# Revit family: Casement_36_C_Side_Hung_Standard
name_source: partatom
category: Windows
revit_build: Autodesk Revit 2014 (Build: 20130308_1515(x64)
units: mm (PartAtom-declared; Revit-internal decimal feet)

## types (12) — shared parameters
Aluminium Thickness = 1 mm  [stored 0.00328084 ft]
Bead SG Gap = 13 mm  [stored 0.0426509 ft]
Casement Dimension = 36 mm  [stored 0.11811 ft]
Custom Sash Left Width = 554 mm  [stored 1.81759 ft]
Custom Sash Right Width = 554 mm  [stored 1.81759 ft]
DG Extrusion Start = 8 mm  [stored 0.0262467 ft]
DG Gasket Finish = Double Glazing Gasket Material
DG Thickness Calc = 4 mm  [stored 0.0131234 ft]
Default Sill Height = 800 mm  [stored 2.62467 ft]
Depth Bead = 22 mm  [stored 0.0721785 ft]
Depth Mullion = 37 mm  [stored 0.121391 ft]
Description = Window 36mm, Type C side hung
Frame Center Offset = 18 mm  [stored 0.0590551 ft]
Limit Fixed Pane Width Max = 1500 mm  [stored 4.92126 ft]
Limit Fixed Pane Width Min = 200 mm  [stored 0.656168 ft]
Limit Sash Height Max = 1300 mm  [stored 4.26509 ft]
Limit Sash Height Min = 300 mm  [stored 0.984252 ft]
Limit Sash Width Max = 600 mm  [stored 1.9685 ft]
Limit Sash Width Min = 300 mm  [stored 0.984252 ft]
Limit Window Height Max = 1346 mm  [stored 4.41601 ft]
Limit Window Height Min = 346 mm
Limit Window Width Max = 2700 mm
Limit Window Width Min = 1400 mm
Manufacturer = Crealco
Max System DG One Piece Thickness = 6 mm  [stored 0.019685 ft]
Max System DG Unit Thickness = 25 mm  [stored 0.082021 ft]
Model = Casement 36
Offset Bead Center Reversed = 18 mm  [stored 0.0590551 ft]
Offset Fixed Panel Left = 600 mm  [stored 1.9685 ft]
Offset Mullion Left Side = 570 mm  [stored 1.87008 ft]
Offset Mullion Right Side = 570 mm  [stored 1.87008 ft]
Offset Sash Side = 23 mm  [stored 0.0754593 ft]
Offset Sash Top = 23 mm  [stored 0.0754593 ft]
Offset Window Exterior = 18 mm  [stored 0.0590551 ft]
SG Gasket Thickness = 6 mm  [stored 0.019685 ft]
Sash Center Offset = 15 mm  [stored 0.0492126 ft]
Sash Overlap = 7 mm  [stored 0.0229659 ft]
Sash Spacing Inner = 8 mm  [stored 0.0262467 ft]
Side Hung Left = Yes
Side Hung Right = No
URL = http://www.crealco.co.za
Wall Closure = By host
Width Bead = 15 mm  [stored 0.0492126 ft]
Width Profile = 30 mm  [stored 0.0984252 ft]
Width Sash Left = 554 mm  [stored 1.81759 ft]
Width Sash Left Opening = 524 mm  [stored 1.71916 ft]
Width Sash Right = 554 mm  [stored 1.81759 ft]
Width Sash Right Opening = 524 mm  [stored 1.71916 ft]
zero-valued in all types: Window Exterior Offset

## per-type parameters (varying)
- 36-1809SS-1000Pa: Area Pane Left=0.35 m²; Area Pane Middle=0.48 m²; Area Pane Right=0.35 m²; Clearvue Insulated LowE SHGC Value=0.485; Clearvue Insulated LowE U Value=3.57; Clearvue Insulated SHGC Value=0.532; Clearvue Insulated U Value=4.09; Clearvue SHGC Value=0.603; Custom Windload=1000 mm  [stored 3.28084 ft]; Custom Window Height=890 mm  [stored 2.91995 ft]; Custom Window Width=1790 mm; Energy Advantage SHGC Value=0.54; Energy Advantage U Value=4.75; Height=890 mm  [stored 2.91995 ft]; Height Fixed Panel Center=830 mm  [stored 2.7231 ft]; Height Sash=814 mm  [stored 2.6706 ft]; Height Sash Opening=844 mm  [stored 2.76903 ft]; Intruderprufe Insulated LowE SHGC Value=0.446; Intruderprufe Insulated LowE U Value=3.5; Intruderprufe Insulated SHGC Value=0.486; Intruderprufe Insulated U Value=3.98; Intruderprufe LowE SHGC Value=0.508; Intruderprufe LowE U Value=4.64; Intruderprufe SHGC Value=0.574; Intruderprufe U Value=6.05; Length Mullion=890 mm  [stored 2.91995 ft]; Max Pane Area=0.48 m²; Mullion Depth Windload Based=37 mm  [stored 0.121391 ft]; Sash Height=845 mm  [stored 2.77231 ft]; Width=1790 mm; Width Fixed Panel Center=590 mm; Windload Design=1000 mm  [stored 3.28084 ft]
- 36-2409SS-1000Pa: Area Pane Left=0.35 m²; Area Pane Middle=0.97 m²; Area Pane Right=0.35 m²; Clearvue Insulated LowE SHGC Value=0.515; Clearvue Insulated LowE U Value=3.31; Clearvue Insulated SHGC Value=0.565; Clearvue Insulated U Value=3.87; Clearvue SHGC Value=0.642; Custom Windload=1000 mm  [stored 3.28084 ft]; Custom Window Height=890 mm  [stored 2.91995 ft]; Custom Window Width=2390 mm; Energy Advantage SHGC Value=0.574; Energy Advantage U Value=4.58; Height=890 mm  [stored 2.91995 ft]; Height Fixed Panel Center=830 mm  [stored 2.7231 ft]; Height Sash=814 mm  [stored 2.6706 ft]; Height Sash Opening=844 mm  [stored 2.76903 ft]; Intruderprufe Insulated LowE SHGC Value=0.473; Intruderprufe Insulated LowE U Value=3.24; Intruderprufe Insulated SHGC Value=0.518; Intruderprufe Insulated U Value=3.78; Intruderprufe LowE SHGC Value=0.539; Intruderprufe LowE U Value=4.47; Intruderprufe SHGC Value=0.61; Intruderprufe U Value=6; Length Mullion=890 mm  [stored 2.91995 ft]; Max Pane Area=0.97 m²; Mullion Depth Windload Based=37 mm  [stored 0.121391 ft]; Sash Height=845 mm  [stored 2.77231 ft]; Width=2390 mm; Width Fixed Panel Center=1190 mm  [stored 3.9042 ft]; Windload Design=1000 mm  [stored 3.28084 ft]
- 36-1812SS-1000Pa: Area Pane Left=0.49 m²; Area Pane Middle=0.65 m²; Area Pane Right=0.49 m²; Clearvue Insulated LowE SHGC Value=0.504; Clearvue Insulated LowE U Value=3.42; Clearvue Insulated SHGC Value=0.554; Clearvue Insulated U Value=3.96; Clearvue SHGC Value=0.628; Custom Windload=1000 mm  [stored 3.28084 ft]; Custom Window Height=1190 mm  [stored 3.9042 ft]; Custom Window Width=1790 mm; Energy Advantage SHGC Value=0.562; Energy Advantage U Value=4.65; Height=1190 mm  [stored 3.9042 ft]; Height Fixed Panel Center=1130 mm  [stored 3.70735 ft]; Height Sash=1114 mm  [stored 3.65486 ft]; Height Sash Opening=1144 mm; Intruderprufe Insulated LowE SHGC Value=0.463; Intruderprufe Insulated LowE U Value=3.35; Intruderprufe Insulated SHGC Value=0.506; Intruderprufe Insulated U Value=3.86; Intruderprufe LowE SHGC Value=0.572; Intruderprufe LowE U Value=4.54; Intruderprufe SHGC Value=0.597; Intruderprufe U Value=6.02; Length Mullion=1190 mm  [stored 3.9042 ft]; Max Pane Area=0.65 m²; Mullion Depth Windload Based=37 mm  [stored 0.121391 ft]; Sash Height=1145 mm  [stored 3.75656 ft]; Width=1790 mm; Width Fixed Panel Center=590 mm; Windload Design=1000 mm  [stored 3.28084 ft]
- 36-2412SS-1000Pa: Area Pane Left=0.49 m²; Area Pane Middle=1.32 m²; Area Pane Right=0.49 m²; Clearvue Insulated LowE SHGC Value=0.534; Clearvue Insulated LowE U Value=3.16; Clearvue Insulated SHGC Value=0.587; Clearvue Insulated U Value=3.75; Clearvue SHGC Value=0.666; Custom Windload=1000 mm  [stored 3.28084 ft]; Custom Window Height=1190 mm  [stored 3.9042 ft]; Custom Window Width=2390 mm; Energy Advantage SHGC Value=0.596; Energy Advantage U Value=4.48; Height=1190 mm  [stored 3.9042 ft]; Height Fixed Panel Center=1130 mm  [stored 3.70735 ft]; Height Sash=1114 mm  [stored 3.65486 ft]; Height Sash Opening=1144 mm; Intruderprufe Insulated LowE SHGC Value=0.49; Intruderprufe Insulated LowE U Value=3.1; Intruderprufe Insulated SHGC Value=0.538; Intruderprufe Insulated U Value=3.66; Intruderprufe LowE SHGC Value=0.558; Intruderprufe LowE U Value=4.38; Intruderprufe SHGC Value=0.633; Intruderprufe U Value=5.97; Length Mullion=1190 mm  [stored 3.9042 ft]; Max Pane Area=1.32 m²; Mullion Depth Windload Based=37 mm  [stored 0.121391 ft]; Sash Height=1145 mm  [stored 3.75656 ft]; Width=2390 mm; Width Fixed Panel Center=1190 mm  [stored 3.9042 ft]; Windload Design=1000 mm  [stored 3.28084 ft]
- 36-1809SS-1500Pa: Area Pane Left=0.35 m²; Area Pane Middle=0.48 m²; Area Pane Right=0.35 m²; Clearvue Insulated LowE SHGC Value=0.485; Clearvue Insulated LowE U Value=3.57; Clearvue Insulated SHGC Value=0.532; Clearvue Insulated U Value=4.09; Clearvue SHGC Value=0.603; Custom Windload=1500 mm  [stored 4.92126 ft]; Custom Window Height=890 mm  [stored 2.91995 ft]; Custom Window Width=1790 mm; Energy Advantage SHGC Value=0.54; Energy Advantage U Value=4.75; Height=890 mm  [stored 2.91995 ft]; Height Fixed Panel Center=830 mm  [stored 2.7231 ft]; Height Sash=814 mm  [stored 2.6706 ft]; Height Sash Opening=844 mm  [stored 2.76903 ft]; Intruderprufe Insulated LowE SHGC Value=0.446; Intruderprufe Insulated LowE U Value=3.5; Intruderprufe Insulated SHGC Value=0.486; Intruderprufe Insulated U Value=3.98; Intruderprufe LowE SHGC Value=0.508; Intruderprufe LowE U Value=4.64; Intruderprufe SHGC Value=0.574; Intruderprufe U Value=6.05; Length Mullion=890 mm  [stored 2.91995 ft]; Max Pane Area=0.48 m²; Mullion Depth Windload Based=37 mm  [stored 0.121391 ft]; Sash Height=845 mm  [stored 2.77231 ft]; Width=1790 mm; Width Fixed Panel Center=590 mm; Windload Design=1500 mm  [stored 4.92126 ft]
- 36-1809SS-2000Pa: Area Pane Left=0.35 m²; Area Pane Middle=0.48 m²; Area Pane Right=0.35 m²; Clearvue Insulated LowE SHGC Value=0.485; Clearvue Insulated LowE U Value=3.57; Clearvue Insulated SHGC Value=0.532; Clearvue Insulated U Value=4.09; Clearvue SHGC Value=0.603; Custom Windload=2000 mm; Custom Window Height=890 mm  [stored 2.91995 ft]; Custom Window Width=1790 mm; Energy Advantage SHGC Value=0.54; Energy Advantage U Value=4.75; Height=890 mm  [stored 2.91995 ft]; Height Fixed Panel Center=830 mm  [stored 2.7231 ft]; Height Sash=814 mm  [stored 2.6706 ft]; Height Sash Opening=844 mm  [stored 2.76903 ft]; Intruderprufe Insulated LowE SHGC Value=0.446; Intruderprufe Insulated LowE U Value=3.5; Intruderprufe Insulated SHGC Value=0.486; Intruderprufe Insulated U Value=3.98; Intruderprufe LowE SHGC Value=0.508; Intruderprufe LowE U Value=4.64; Intruderprufe SHGC Value=0.574; Intruderprufe U Value=6.05; Length Mullion=890 mm  [stored 2.91995 ft]; Max Pane Area=0.48 m²; Mullion Depth Windload Based=37 mm  [stored 0.121391 ft]; Sash Height=845 mm  [stored 2.77231 ft]; Width=1790 mm; Width Fixed Panel Center=590 mm; Windload Design=2000 mm
- 36-2409SS-1500Pa: Area Pane Left=0.35 m²; Area Pane Middle=0.97 m²; Area Pane Right=0.35 m²; Clearvue Insulated LowE SHGC Value=0.515; Clearvue Insulated LowE U Value=3.31; Clearvue Insulated SHGC Value=0.565; Clearvue Insulated U Value=3.87; Clearvue SHGC Value=0.642; Custom Windload=1500 mm  [stored 4.92126 ft]; Custom Window Height=890 mm  [stored 2.91995 ft]; Custom Window Width=2390 mm; Energy Advantage SHGC Value=0.574; Energy Advantage U Value=4.58; Height=890 mm  [stored 2.91995 ft]; Height Fixed Panel Center=830 mm  [stored 2.7231 ft]; Height Sash=814 mm  [stored 2.6706 ft]; Height Sash Opening=844 mm  [stored 2.76903 ft]; Intruderprufe Insulated LowE SHGC Value=0.473; Intruderprufe Insulated LowE U Value=3.24; Intruderprufe Insulated SHGC Value=0.518; Intruderprufe Insulated U Value=3.78; Intruderprufe LowE SHGC Value=0.539; Intruderprufe LowE U Value=4.47; Intruderprufe SHGC Value=0.61; Intruderprufe U Value=6; Length Mullion=890 mm  [stored 2.91995 ft]; Max Pane Area=0.97 m²; Mullion Depth Windload Based=37 mm  [stored 0.121391 ft]; Sash Height=845 mm  [stored 2.77231 ft]; Width=2390 mm; Width Fixed Panel Center=1190 mm  [stored 3.9042 ft]; Windload Design=1500 mm  [stored 4.92126 ft]
- 36-2409SS-2000Pa: Area Pane Left=0.35 m²; Area Pane Middle=0.97 m²; Area Pane Right=0.35 m²; Clearvue Insulated LowE SHGC Value=0.515; Clearvue Insulated LowE U Value=3.31; Clearvue Insulated SHGC Value=0.565; Clearvue Insulated U Value=3.87; Clearvue SHGC Value=0.642; Custom Windload=2000 mm; Custom Window Height=890 mm  [stored 2.91995 ft]; Custom Window Width=2390 mm; Energy Advantage SHGC Value=0.574; Energy Advantage U Value=4.58; Height=890 mm  [stored 2.91995 ft]; Height Fixed Panel Center=830 mm  [stored 2.7231 ft]; Height Sash=814 mm  [stored 2.6706 ft]; Height Sash Opening=844 mm  [stored 2.76903 ft]; Intruderprufe Insulated LowE SHGC Value=0.473; Intruderprufe Insulated LowE U Value=3.24; Intruderprufe Insulated SHGC Value=0.518; Intruderprufe Insulated U Value=3.78; Intruderprufe LowE SHGC Value=0.539; Intruderprufe LowE U Value=4.47; Intruderprufe SHGC Value=0.61; Intruderprufe U Value=6; Length Mullion=890 mm  [stored 2.91995 ft]; Max Pane Area=0.97 m²; Mullion Depth Windload Based=37 mm  [stored 0.121391 ft]; Sash Height=845 mm  [stored 2.77231 ft]; Width=2390 mm; Width Fixed Panel Center=1190 mm  [stored 3.9042 ft]; Windload Design=2000 mm
- 36-1812SS-1500Pa: Area Pane Left=0.49 m²; Area Pane Middle=0.65 m²; Area Pane Right=0.49 m²; Clearvue Insulated LowE SHGC Value=0.504; Clearvue Insulated LowE U Value=3.42; Clearvue Insulated SHGC Value=0.554; Clearvue Insulated U Value=3.96; Clearvue SHGC Value=0.628; Custom Windload=1500 mm  [stored 4.92126 ft]; Custom Window Height=1190 mm  [stored 3.9042 ft]; Custom Window Width=1790 mm; Energy Advantage SHGC Value=0.562; Energy Advantage U Value=4.65; Height=1190 mm  [stored 3.9042 ft]; Height Fixed Panel Center=1130 mm  [stored 3.70735 ft]; Height Sash=1114 mm  [stored 3.65486 ft]; Height Sash Opening=1144 mm; Intruderprufe Insulated LowE SHGC Value=0.463; Intruderprufe Insulated LowE U Value=3.35; Intruderprufe Insulated SHGC Value=0.506; Intruderprufe Insulated U Value=3.86; Intruderprufe LowE SHGC Value=0.572; Intruderprufe LowE U Value=4.54; Intruderprufe SHGC Value=0.597; Intruderprufe U Value=6.02; Length Mullion=1190 mm  [stored 3.9042 ft]; Max Pane Area=0.65 m²; Mullion Depth Windload Based=37 mm  [stored 0.121391 ft]; Sash Height=1145 mm  [stored 3.75656 ft]; Width=1790 mm; Width Fixed Panel Center=590 mm; Windload Design=1500 mm  [stored 4.92126 ft]
- 36-1812SS-2000Pa: Area Pane Left=0.49 m²; Area Pane Middle=0.65 m²; Area Pane Right=0.49 m²; Clearvue Insulated LowE SHGC Value=0.501; Clearvue Insulated LowE U Value=3.51; Clearvue Insulated SHGC Value=0.551; Clearvue Insulated U Value=4.05; Clearvue SHGC Value=0.626; Custom Windload=2000 mm; Custom Window Height=1190 mm  [stored 3.9042 ft]; Custom Window Width=1790 mm; Energy Advantage SHGC Value=0.561; Energy Advantage U Value=4.72; Height=1190 mm  [stored 3.9042 ft]; Height Fixed Panel Center=1130 mm  [stored 3.70735 ft]; Height Sash=1114 mm  [stored 3.65486 ft]; Height Sash Opening=1144 mm; Intruderprufe Insulated LowE SHGC Value=0.464; Intruderprufe Insulated LowE U Value=3.44; Intruderprufe Insulated SHGC Value=0.506; Intruderprufe Insulated U Value=3.95; Intruderprufe LowE SHGC Value=0.524; Intruderprufe LowE U Value=4.62; Intruderprufe SHGC Value=0.596; Intruderprufe U Value=6.08; Length Mullion=1190 mm  [stored 3.9042 ft]; Max Pane Area=0.65 m²; Mullion Depth Windload Based=54 mm  [stored 0.177165 ft]; Sash Height=1145 mm  [stored 3.75656 ft]; Width=1790 mm; Width Fixed Panel Center=590 mm; Windload Design=2000 mm
- 36-2412SS-1500Pa: Area Pane Left=0.49 m²; Area Pane Middle=1.32 m²; Area Pane Right=0.49 m²; Clearvue Insulated LowE SHGC Value=0.532; Clearvue Insulated LowE U Value=3.23; Clearvue Insulated SHGC Value=0.585; Clearvue Insulated U Value=3.81; Clearvue SHGC Value=0.665; Custom Windload=1500 mm  [stored 4.92126 ft]; Custom Window Height=1190 mm  [stored 3.9042 ft]; Custom Window Width=2390 mm; Energy Advantage SHGC Value=0.595; Energy Advantage U Value=4.54; Height=1190 mm  [stored 3.9042 ft]; Height Fixed Panel Center=1130 mm  [stored 3.70735 ft]; Height Sash=1114 mm  [stored 3.65486 ft]; Height Sash Opening=1144 mm; Intruderprufe Insulated LowE SHGC Value=0.491; Intruderprufe Insulated LowE U Value=3.17; Intruderprufe Insulated SHGC Value=0.538; Intruderprufe Insulated U Value=3.72; Intruderprufe LowE SHGC Value=0.556; Intruderprufe LowE U Value=4.44; Intruderprufe SHGC Value=0.632; Intruderprufe U Value=6.02; Length Mullion=1190 mm  [stored 3.9042 ft]; Max Pane Area=1.32 m²; Mullion Depth Windload Based=54 mm  [stored 0.177165 ft]; Sash Height=1145 mm  [stored 3.75656 ft]; Width=2390 mm; Width Fixed Panel Center=1190 mm  [stored 3.9042 ft]; Windload Design=1500 mm  [stored 4.92126 ft]
- 36-2412SS-2000Pa: Area Pane Left=0.49 m²; Area Pane Middle=1.32 m²; Area Pane Right=0.49 m²; Clearvue Insulated LowE SHGC Value=0.532; Clearvue Insulated LowE U Value=3.23; Clearvue Insulated SHGC Value=0.585; Clearvue Insulated U Value=3.81; Clearvue SHGC Value=0.665; Custom Windload=2000 mm; Custom Window Height=1190 mm  [stored 3.9042 ft]; Custom Window Width=2390 mm; Energy Advantage SHGC Value=0.595; Energy Advantage U Value=4.54; Height=1190 mm  [stored 3.9042 ft]; Height Fixed Panel Center=1130 mm  [stored 3.70735 ft]; Height Sash=1114 mm  [stored 3.65486 ft]; Height Sash Opening=1144 mm; Intruderprufe Insulated LowE SHGC Value=0.491; Intruderprufe Insulated LowE U Value=3.17; Intruderprufe Insulated SHGC Value=0.538; Intruderprufe Insulated U Value=3.72; Intruderprufe LowE SHGC Value=0.556; Intruderprufe LowE U Value=4.44; Intruderprufe SHGC Value=0.632; Intruderprufe U Value=6.02; Length Mullion=1190 mm  [stored 3.9042 ft]; Max Pane Area=1.32 m²; Mullion Depth Windload Based=54 mm  [stored 0.177165 ft]; Sash Height=1145 mm  [stored 3.75656 ft]; Width=2390 mm; Width Fixed Panel Center=1190 mm  [stored 3.9042 ft]; Windload Design=2000 mm

note: [stored X ft] marks values corroborated as IEEE doubles in the binary element streams (Revit-internal decimal feet)

## geometry (parser evidence)
native form markers: Extrusion x1, Sweep x29
no freeform markers — native parametric forms only
